# Revit family: PRD_FrankeWS_SoapDpnsrs_SoapDispenser_SD80
name_source: partatom
category: Specialty Equipment
revit_build: Autodesk Revit 2018 (Build: 20190510_1515(x64)
units: mm (PartAtom-declared; Revit-internal decimal feet)

## family parameters
Cut with Voids When Loaded = No
Host = Face
OmniClass Number = 23.40.20.21.34
OmniClass Title = Soap Holders, Dispensers
Part Type = Normal
Room Calculation Point = No
Round Connector Dimension = Use Diameter
Shared = No

## types (1)
- SD80
    AssetType = Fixed
    BIMObjectName = PRD_AR_SoapDispensers_SoapDispenser_SD80
    Category = Pr_40_70_22_81, Soap dispensers
    Color = Chrome
    Default Elevation = 0 mm  [stored 0 ft]
    Description = Soap dispenser for table top mounting into worktops with max. 45 mm thickness, high polished chromated brass, requires 22 mm drilling hole, 1/2inch. thread, spout not movable, spout length 140 mm, suitable for liquid soaps and lotions, 1 liter soap tank with membrane for pressure balance, filled from above. with standard body lenght (85 mm)
    DurationUnit = year
    Features = brass, chromed, counter top mounting, 44x400x162 mm (WxHxD)
    Finish = High polished
    Form = Table top mounted into worktops
    GrossWeight = 1.16 kg
    IfcExportAs = IfcFurnitureType
    IfcExportType = NOTDEFINED
    MainColor = Stainless steel
    Manufacturer = KWC Group AG
    ManufacturerName = KWC Group AG
    ManufacturerURL = www.kwc.com
    Material = Brass
    MaterialsBody = Brass
    MaterialsFinishAndColour = High polished chromated brass
    Model = SD80
    ModelNumber = 2000056721
    ModelReference = SD80
    NBSDescription = Soap dispensers
    NBSReference = 45-35-72/358
    Name = Soap dispenser SD80
    NetWeight = 1.00 kg
    NominalDepth = 162 mm  [stored 0.531496 ft]
    NominalHeight = 400 mm  [stored 1.31234 ft]
    NominalLength = 44 mm  [stored 0.144357 ft]
    NominalWidth = 44 mm  [stored 0.144357 ft]
    Operation = Manual
    ProductInformation = https://pim.kwc.com
    Shape = Cylindrical
    Size = 44 x 400 x 162 mm
    SoapDispenserMaterial = PRD_AR_ChromatedBrass_HighPolished
    Style = Soap dispenser
    TypeOfConsumable = Liquid soap
    TypeOfSoapContainer = Integrated refillable tank
    URL = www.kwc.com
    Uniclass2015Code = Pr_40_70_22_81
    Uniclass2015Title = Soap dispensers
    Uniclass2015Version = Products v1.5
    Version = 1
    WarrantyDurationUnit = year

note: [stored X ft] marks values corroborated as IEEE doubles in the binary element streams (Revit-internal decimal feet)

## geometry (parser evidence)
native form markers: Sweep x2
no freeform markers — native parametric forms only
